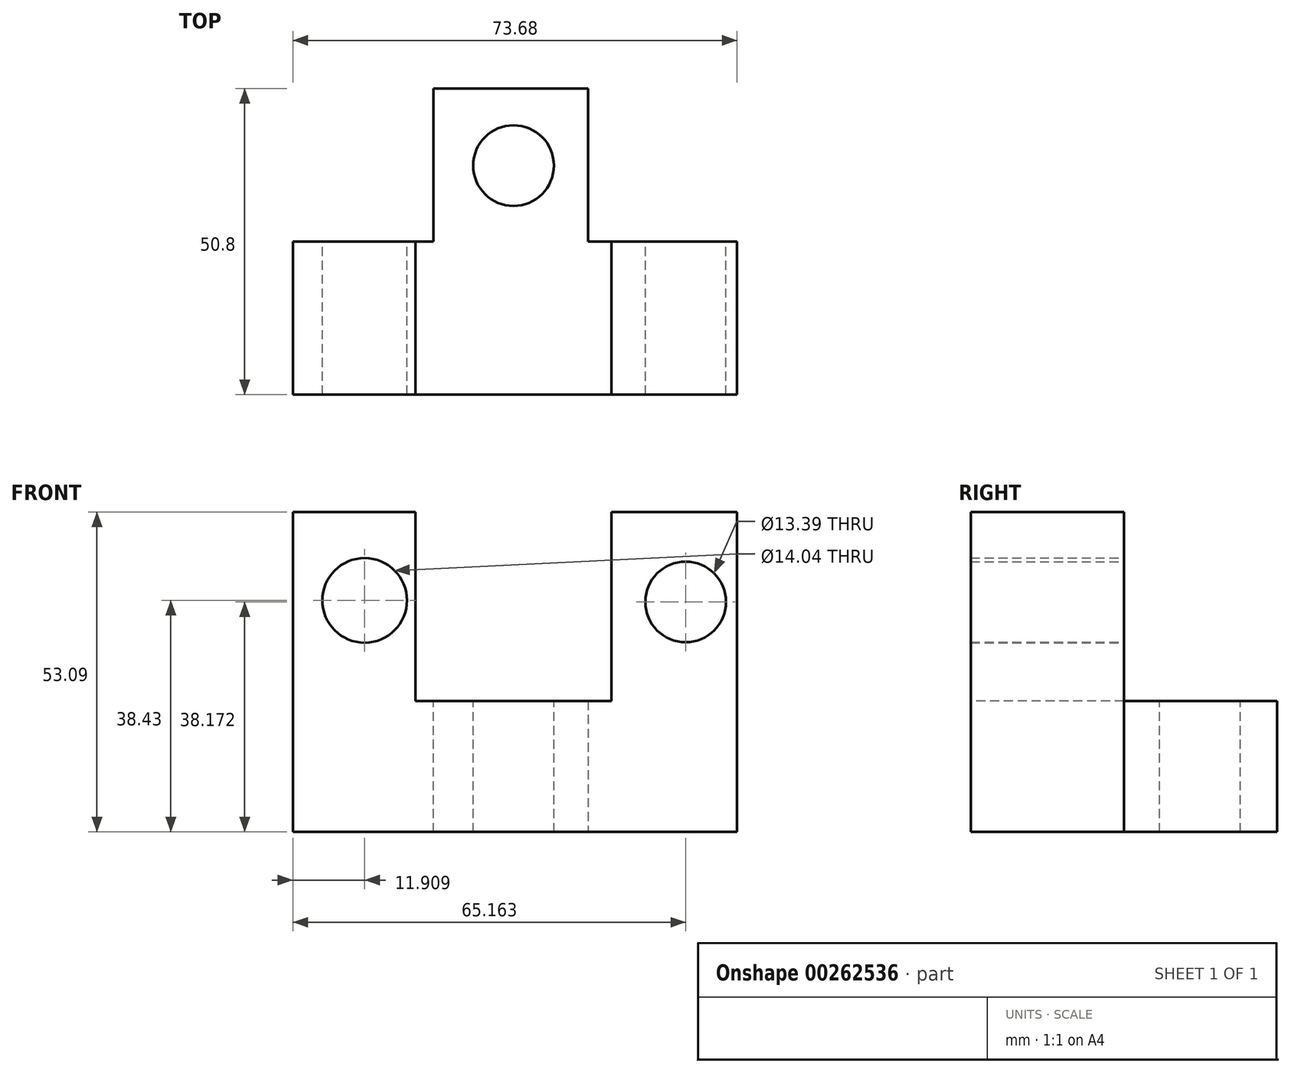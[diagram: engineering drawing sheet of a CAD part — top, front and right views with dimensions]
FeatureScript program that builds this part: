
annotation { "Feature Type Name" : "Feature", "Feature Type Description" : "" }
export const myFeature = defineFeature(function(context is Context, id is Id, definition is map)
    precondition{}
    {
        {
            var Q0;
            Q0=qCreatedBy(makeId("Front.planeOp"),FACE);
            var sketch = newSketch(context, id + "F0", { "sketchPlane" : qUnion([Q0])});
            skLineSegment(sketch, "E0", {"start": v(-46.64, 28.9) * mm, "end": v(-46.64, -21.7) * mm});
            skLineSegment(sketch, "E1", {"start": v(-46.64, -21.7) * mm, "end": v(27.04, -21.7) * mm});
            skLineSegment(sketch, "E2", {"start": v(27.04, -21.7) * mm, "end": v(27.04, 31.38) * mm});
            skLineSegment(sketch, "E3", {"start": v(27.04, 31.38) * mm, "end": v(-46.64, 31.38) * mm});
            skLineSegment(sketch, "E4", {"start": v(-46.64, 31.38) * mm, "end": v(-46.64, 28.9) * mm});
            skSolve(sketch);
        }
        {
            var Q0;
            Q0=makeQuery(id+"F0.imprint","IMPRINT",FACE,{"disambiguationData":[TD([[makeQuery(id+"F0.imprint","IMPRINT",EDGE,{"derivedFrom":sQuery(id+"F0.wireOp",EDGE,"E0")}),1.0]])]});
            extrude(context, id + "F1", {"entities" : qUnion([Q0]), "depth" : 25.4 * mm});
        }
        {
            var Q0;
            Q0=makeQuery(id+"F1.opExtrude","CAP_FACE",FACE,{"disambiguationData":[OSD([sQuery(id+"F0.wireOp",EDGE,"E0"),sQuery(id+"F0.wireOp",EDGE,"E1"),sQuery(id+"F0.wireOp",EDGE,"E2"),sQuery(id+"F0.wireOp",EDGE,"E3"),sQuery(id+"F0.wireOp",EDGE,"E4")])],"isStart":false});
            var sketch = newSketch(context, id + "F2", { "sketchPlane" : qUnion([Q0])});
            skLineSegment(sketch, "E5", {"start": v(-26.3, 31.38) * mm, "end": v(-26.3, 0) * mm});
            skLineSegment(sketch, "E6", {"start": v(-26.3, 0) * mm, "end": v(6.2, 0) * mm});
            skLineSegment(sketch, "E7", {"start": v(6.2, 0) * mm, "end": v(6.2, 31.38) * mm});
            skLineSegment(sketch, "E8", {"start": v(6.2, 31.38) * mm, "end": v(-26.3, 31.38) * mm});
            skSolve(sketch);
        }
        {
            var Q0;
            Q0=makeQuery(id+"F2.imprint","IMPRINT",FACE,{"disambiguationData":[TD([[makeQuery(id+"F2.imprint","IMPRINT",EDGE,{"derivedFrom":sQuery(id+"F2.wireOp",EDGE,"E5")}),1.0]])]});
            extrude(context, id + "F3", {"entities" : qUnion([Q0]), "operationType" : NewBodyOperationType.REMOVE, "oppositeDirection" : true, "depth" : 76.2 * mm});
        }
        {
            var Q0;
            Q0=makeQuery(id+"F1.opExtrude","CAP_FACE",FACE,{"disambiguationData":[OSD([sQuery(id+"F0.wireOp",EDGE,"E0"),sQuery(id+"F0.wireOp",EDGE,"E1"),sQuery(id+"F0.wireOp",EDGE,"E2"),sQuery(id+"F0.wireOp",EDGE,"E3"),sQuery(id+"F0.wireOp",EDGE,"E4")])],"isStart":true});
            var sketch = newSketch(context, id + "F4", { "sketchPlane" : qUnion([Q0])});
            skLineSegment(sketch, "E9", {"start": v(-2.33, 0) * mm, "end": v(-2.33, -21.7) * mm});
            skLineSegment(sketch, "E10", {"start": v(-2.33, -21.7) * mm, "end": v(23.31, -21.7) * mm});
            skLineSegment(sketch, "E11", {"start": v(23.31, -21.7) * mm, "end": v(23.31, 0) * mm});
            skLineSegment(sketch, "E12", {"start": v(23.31, 0) * mm, "end": v(-2.33, 0) * mm});
            skSolve(sketch);
        }
        {
            var Q0;
            Q0=makeQuery(id+"F4.imprint","IMPRINT",FACE,{"disambiguationData":[TD([[makeQuery(id+"F4.imprint","IMPRINT",EDGE,{"derivedFrom":sQuery(id+"F4.wireOp",EDGE,"E9")}),1.0]])]});
            extrude(context, id + "F5", {"entities" : qUnion([Q0]), "operationType" : NewBodyOperationType.ADD, "depth" : 25.4 * mm});
        }
        {
            var Q0;
            {var subQ0=sQuery(id+"F0.wireOp",EDGE,"E3");var subQ1=sQuery(id+"F0.wireOp",EDGE,"E2");var subQ2=sQuery(id+"F0.wireOp",EDGE,"E1");Q0=makeQuery(id+"F5.boolean.opBoolean","SPLIT",FACE,{"disambiguationData":[TD([makeQuery(id+"F1.opExtrude","SWEPT_FACE",FACE,{"disambiguationData":[OSD([subQ1])]})])],"derivedFrom":makeQuery(id+"F1.opExtrude","CAP_FACE",FACE,{"disambiguationData":[OSD([sQuery(id+"F0.wireOp",EDGE,"E0"),subQ2,subQ1,subQ0,sQuery(id+"F0.wireOp",EDGE,"E4")])],"isStart":true})});}
            var sketch = newSketch(context, id + "F6", { "sketchPlane" : qUnion([Q0])});
            skCircle(sketch, "E13", {"center": v(-18.52, 16.46) * mm, "radius": 6.7 * mm});
            skSolve(sketch);
        }
        {
            var Q0;
            {var subQ0=sQuery(id+"F0.wireOp",EDGE,"E3");var subQ1=sQuery(id+"F0.wireOp",EDGE,"E1");var subQ2=sQuery(id+"F0.wireOp",EDGE,"E4");var subQ3=sQuery(id+"F0.wireOp",EDGE,"E0");Q0=makeQuery(id+"F5.boolean.opBoolean","SPLIT",FACE,{"disambiguationData":[TD([makeQuery(id+"F3.boolean.opBoolean","COPY",FACE,{"derivedFrom":makeQuery(id+"F3.opExtrude","SWEPT_FACE",FACE,{"disambiguationData":[OSD([sQuery(id+"F2.wireOp",EDGE,"E5")])]})})])],"derivedFrom":makeQuery(id+"F1.opExtrude","CAP_FACE",FACE,{"disambiguationData":[OSD([subQ3,subQ1,sQuery(id+"F0.wireOp",EDGE,"E2"),subQ0,subQ2])],"isStart":true})});}
            var sketch = newSketch(context, id + "F7", { "sketchPlane" : qUnion([Q0])});
            skCircle(sketch, "E14", {"center": v(34.73, 16.72) * mm, "radius": 7.02 * mm});
            skSolve(sketch);
        }
        {
            var Q0;
            Q0=makeQuery(id+"F5.boolean.opBoolean","MERGE",FACE,{"derivedFrom":[makeQuery(id+"F3.boolean.opBoolean","COPY",FACE,{"derivedFrom":makeQuery(id+"F3.opExtrude","SWEPT_FACE",FACE,{"disambiguationData":[OSD([sQuery(id+"F2.wireOp",EDGE,"E6")])]})}),makeQuery(id+"F5.opExtrude","SWEPT_FACE",FACE,{"disambiguationData":[OSD([sQuery(id+"F4.wireOp",EDGE,"E12")])]})]});
            var sketch = newSketch(context, id + "F8", { "sketchPlane" : qUnion([Q0])});
            skCircle(sketch, "E15", {"center": v(-10.03, 12.6) * mm, "radius": 6.7 * mm});
            skSolve(sketch);
        }
        {
            var Q0;
            Q0 = qSketchRegion(id + "F8", true);
            extrude(context, id + "F9", {"entities" : qUnion([Q0]), "operationType" : NewBodyOperationType.REMOVE, "oppositeDirection" : true, "depth" : 25.4 * mm});
        }
        {
            var Q0;
            Q0 = qSketchRegion(id + "F6", true);
            extrude(context, id + "F10", {"entities" : qUnion([Q0]), "operationType" : NewBodyOperationType.REMOVE, "oppositeDirection" : true, "depth" : 25.4 * mm});
        }
        {
            var Q0;
            Q0 = qSketchRegion(id + "F7", true);
            extrude(context, id + "F11", {"entities" : qUnion([Q0]), "operationType" : NewBodyOperationType.REMOVE, "oppositeDirection" : true, "depth" : 25.4 * mm});
        }
    });
